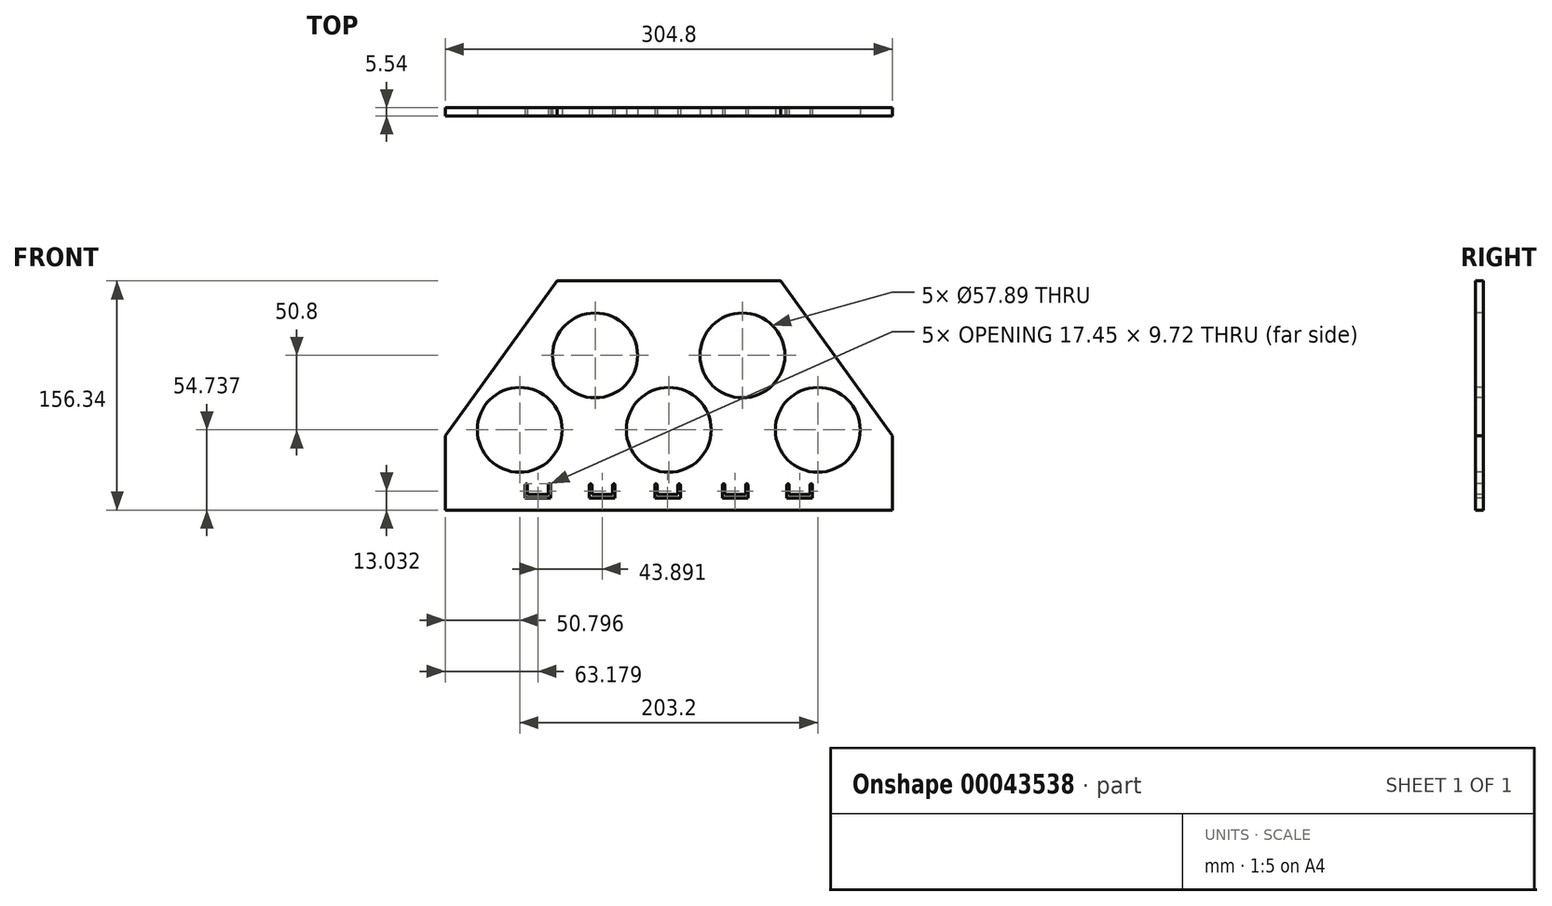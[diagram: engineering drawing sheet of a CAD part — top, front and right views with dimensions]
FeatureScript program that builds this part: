
annotation { "Feature Type Name" : "Feature", "Feature Type Description" : "" }
export const myFeature = defineFeature(function(context is Context, id is Id, definition is map)
    precondition{}
    {
        {
            var Q0;
            Q0=qCreatedBy(makeId("Front.planeOp"),FACE);
            var sketch = newSketch(context, id + "F0", { "sketchPlane" : qUnion([Q0])});
            skLineSegment(sketch, "E0", {"start": v(-67.22, 104.18) * mm, "end": v(85.18, 104.18) * mm});
            skLineSegment(sketch, "E1", {"start": v(85.18, 104.18) * mm, "end": v(161.38, -1.36) * mm});
            skLineSegment(sketch, "E2", {"start": v(161.38, -1.36) * mm, "end": v(161.38, -52.16) * mm});
            skLineSegment(sketch, "E3", {"start": v(161.38, -52.16) * mm, "end": v(-143.42, -52.16) * mm});
            skLineSegment(sketch, "E4", {"start": v(-143.42, -52.16) * mm, "end": v(-143.42, -1.36) * mm});
            skLineSegment(sketch, "E5", {"start": v(-143.42, -1.36) * mm, "end": v(-67.22, 104.18) * mm});
            skSolve(sketch);
        }
        {
            var Q0;
            Q0=makeQuery(id+"F0.imprint","IMPRINT",FACE,{"disambiguationData":[TD([[makeQuery(id+"F0.imprint","IMPRINT",EDGE,{"derivedFrom":sQuery(id+"F0.wireOp",EDGE,"E0")}),-1.0]])]});
            extrude(context, id + "F1", {"entities" : qUnion([Q0]), "depth" : 5.54 * mm});
        }
        {
            var Q0;
            Q0=makeQuery(id+"F1.opExtrude","CAP_FACE",FACE,{"disambiguationData":[OSD([sQuery(id+"F0.wireOp",EDGE,"E0"),sQuery(id+"F0.wireOp",EDGE,"E1"),sQuery(id+"F0.wireOp",EDGE,"E2"),sQuery(id+"F0.wireOp",EDGE,"E3"),sQuery(id+"F0.wireOp",EDGE,"E4"),sQuery(id+"F0.wireOp",EDGE,"E5")])],"isStart":false});
            var sketch = newSketch(context, id + "F2", { "sketchPlane" : qUnion([Q0])});
            skPoint(sketch, "E6", {"position": v(-41.24, 53.38) * mm});
            skPoint(sketch, "E7", {"position": v(59.2, 53.38) * mm});
            skPoint(sketch, "E8", {"position": v(8.98, 2.58) * mm});
            skPoint(sketch, "E9", {"position": v(-92.62, 2.58) * mm});
            skPoint(sketch, "E10", {"position": v(110.58, 2.58) * mm});
            skSolve(sketch);
        }
        {
            var Q0;
            Q0=sQuery(id+"F2.wireOp",VERTEX,"E6");
            var Q1;
            Q1=sQuery(id+"F2.wireOp",VERTEX,"E7");
            var Q2;
            Q2=sQuery(id+"F2.wireOp",VERTEX,"E10");
            var Q3;
            Q3=sQuery(id+"F2.wireOp",VERTEX,"E8");
            var Q4;
            Q4=sQuery(id+"F2.wireOp",VERTEX,"E9");
            var Q5;
            Q5=makeQuery(id+"F1.opExtrude","SWEPT_BODY",BODY,{"disambiguationData":[OSD([sQuery(id+"F0.wireOp",EDGE,"E0"),sQuery(id+"F0.wireOp",EDGE,"E1"),sQuery(id+"F0.wireOp",EDGE,"E2"),sQuery(id+"F0.wireOp",EDGE,"E3"),sQuery(id+"F0.wireOp",EDGE,"E4"),sQuery(id+"F0.wireOp",EDGE,"E5")])]});
            hole(context, id + "F3", {"style" : HoleStyle.SIMPLE, "holeDiameter" : 57.9 * mm, "endStyle" : HoleEndStyle.THROUGH, "locations" : qUnion([Q0, Q1, Q2, Q3, Q4]), "scope" : qUnion([Q5])});
        }
        {
            var Q0;
            Q0=makeQuery(id+"F1.opExtrude","CAP_FACE",FACE,{"disambiguationData":[OSD([sQuery(id+"F0.wireOp",EDGE,"E0"),sQuery(id+"F0.wireOp",EDGE,"E1"),sQuery(id+"F0.wireOp",EDGE,"E2"),sQuery(id+"F0.wireOp",EDGE,"E3"),sQuery(id+"F0.wireOp",EDGE,"E4"),sQuery(id+"F0.wireOp",EDGE,"E5")])],"isStart":false});
            var sketch = newSketch(context, id + "F4", { "sketchPlane" : qUnion([Q0])});
            skLineSegment(sketch, "E11", {"start": v(-88.97, -35.1) * mm, "end": v(-88.97, -43.99) * mm});
            skLineSegment(sketch, "E12", {"start": v(-88.97, -43.99) * mm, "end": v(-71.52, -43.99) * mm});
            skLineSegment(sketch, "E13", {"start": v(-71.52, -43.99) * mm, "end": v(-71.52, -35.1) * mm});
            skLineSegment(sketch, "E14", {"start": v(-87.32, -35.1) * mm, "end": v(-87.32, -41.6) * mm});
            skLineSegment(sketch, "E15", {"start": v(-87.32, -41.6) * mm, "end": v(-73.17, -41.6) * mm});
            skLineSegment(sketch, "E16", {"start": v(-73.17, -41.6) * mm, "end": v(-73.17, -35.1) * mm});
            skArc(sketch, "E17", {"start": v(-87.32, -35.1) * mm, "mid": v(-88.14, -34.27) * mm, "end": v(-88.97, -35.1) * mm});
            skArc(sketch, "E18", {"start": v(-71.52, -35.1) * mm, "mid": v(-72.34, -34.27) * mm, "end": v(-73.17, -35.1) * mm});
            skSolve(sketch);
        }
        {
            var Q0;
            Q0=makeQuery(id+"F4.imprint","IMPRINT",FACE,{"disambiguationData":[TD([[makeQuery(id+"F4.imprint","IMPRINT",EDGE,{"derivedFrom":sQuery(id+"F4.wireOp",EDGE,"E11")}),1.0]])]});
            extrude(context, id + "F5", {"entities" : qUnion([Q0]), "operationType" : NewBodyOperationType.REMOVE, "endBound" : BoundingType.THROUGH_ALL, "oppositeDirection" : true, "depth" : 25.4 * mm});
        }
        {
            var Q0;
            Q0=makeQuery(id+"F1.opExtrude","CAP_FACE",FACE,{"disambiguationData":[OSD([sQuery(id+"F0.wireOp",EDGE,"E0"),sQuery(id+"F0.wireOp",EDGE,"E1"),sQuery(id+"F0.wireOp",EDGE,"E2"),sQuery(id+"F0.wireOp",EDGE,"E3"),sQuery(id+"F0.wireOp",EDGE,"E4"),sQuery(id+"F0.wireOp",EDGE,"E5")])],"isStart":false});
            var sketch = newSketch(context, id + "F6", { "sketchPlane" : qUnion([Q0])});
            skLineSegment(sketch, "E19", {"start": v(-45.08, -35.1) * mm, "end": v(-45.08, -43.99) * mm});
            skLineSegment(sketch, "E20", {"start": v(-45.08, -43.99) * mm, "end": v(-27.63, -43.99) * mm});
            skLineSegment(sketch, "E21", {"start": v(-27.63, -43.99) * mm, "end": v(-27.63, -35.1) * mm});
            skLineSegment(sketch, "E22", {"start": v(-43.42, -35.1) * mm, "end": v(-43.42, -41.6) * mm});
            skLineSegment(sketch, "E23", {"start": v(-43.42, -41.6) * mm, "end": v(-29.28, -41.6) * mm});
            skLineSegment(sketch, "E24", {"start": v(-29.28, -41.6) * mm, "end": v(-29.28, -35.1) * mm});
            skArc(sketch, "E25", {"start": v(-43.42, -35.1) * mm, "mid": v(-44.25, -34.27) * mm, "end": v(-45.08, -35.1) * mm});
            skArc(sketch, "E26", {"start": v(-27.63, -35.1) * mm, "mid": v(-28.45, -34.27) * mm, "end": v(-29.28, -35.1) * mm});
            skSolve(sketch);
        }
        {
            var Q0;
            Q0=makeQuery(id+"F6.imprint","IMPRINT",FACE,{"disambiguationData":[TD([[makeQuery(id+"F6.imprint","IMPRINT",EDGE,{"derivedFrom":sQuery(id+"F6.wireOp",EDGE,"E19")}),1.0]])]});
            extrude(context, id + "F7", {"entities" : qUnion([Q0]), "operationType" : NewBodyOperationType.REMOVE, "oppositeDirection" : true, "depth" : 17.76 * mm});
        }
        {
            var Q0;
            Q0=makeQuery(id+"F1.opExtrude","CAP_FACE",FACE,{"disambiguationData":[OSD([sQuery(id+"F0.wireOp",EDGE,"E0"),sQuery(id+"F0.wireOp",EDGE,"E1"),sQuery(id+"F0.wireOp",EDGE,"E2"),sQuery(id+"F0.wireOp",EDGE,"E3"),sQuery(id+"F0.wireOp",EDGE,"E4"),sQuery(id+"F0.wireOp",EDGE,"E5")])],"isStart":false});
            var sketch = newSketch(context, id + "F8", { "sketchPlane" : qUnion([Q0])});
            skLineSegment(sketch, "E27", {"start": v(-0.57, -35.1) * mm, "end": v(-0.57, -43.99) * mm});
            skLineSegment(sketch, "E28", {"start": v(-0.57, -43.99) * mm, "end": v(16.88, -43.99) * mm});
            skLineSegment(sketch, "E29", {"start": v(16.88, -43.99) * mm, "end": v(16.88, -35.1) * mm});
            skLineSegment(sketch, "E30", {"start": v(1.08, -35.1) * mm, "end": v(1.08, -41.6) * mm});
            skLineSegment(sketch, "E31", {"start": v(1.08, -41.6) * mm, "end": v(15.22, -41.6) * mm});
            skLineSegment(sketch, "E32", {"start": v(15.22, -41.6) * mm, "end": v(15.22, -35.1) * mm});
            skArc(sketch, "E33", {"start": v(1.08, -35.1) * mm, "mid": v(0.25, -34.27) * mm, "end": v(-0.57, -35.1) * mm});
            skArc(sketch, "E34", {"start": v(16.88, -35.1) * mm, "mid": v(16.05, -34.27) * mm, "end": v(15.22, -35.1) * mm});
            skSolve(sketch);
        }
        {
            var Q0;
            Q0=makeQuery(id+"F8.imprint","IMPRINT",FACE,{"disambiguationData":[TD([[makeQuery(id+"F8.imprint","IMPRINT",EDGE,{"derivedFrom":sQuery(id+"F8.wireOp",EDGE,"E27")}),1.0]])]});
            extrude(context, id + "F9", {"entities" : qUnion([Q0]), "operationType" : NewBodyOperationType.REMOVE, "oppositeDirection" : true, "depth" : 25.4 * mm});
        }
        {
            var Q0;
            Q0=makeQuery(id+"F1.opExtrude","CAP_FACE",FACE,{"disambiguationData":[OSD([sQuery(id+"F0.wireOp",EDGE,"E0"),sQuery(id+"F0.wireOp",EDGE,"E1"),sQuery(id+"F0.wireOp",EDGE,"E2"),sQuery(id+"F0.wireOp",EDGE,"E3"),sQuery(id+"F0.wireOp",EDGE,"E4"),sQuery(id+"F0.wireOp",EDGE,"E5")])],"isStart":false});
            var sketch = newSketch(context, id + "F10", { "sketchPlane" : qUnion([Q0])});
            skLineSegment(sketch, "E35", {"start": v(45.58, -35.1) * mm, "end": v(45.58, -43.99) * mm});
            skLineSegment(sketch, "E36", {"start": v(45.58, -43.99) * mm, "end": v(63.03, -43.99) * mm});
            skLineSegment(sketch, "E37", {"start": v(63.03, -43.99) * mm, "end": v(63.03, -35.1) * mm});
            skLineSegment(sketch, "E38", {"start": v(47.23, -35.1) * mm, "end": v(47.23, -41.6) * mm});
            skLineSegment(sketch, "E39", {"start": v(47.23, -41.6) * mm, "end": v(61.38, -41.6) * mm});
            skLineSegment(sketch, "E40", {"start": v(61.38, -41.6) * mm, "end": v(61.38, -35.1) * mm});
            skArc(sketch, "E41", {"start": v(47.23, -35.1) * mm, "mid": v(46.4, -34.27) * mm, "end": v(45.58, -35.1) * mm});
            skArc(sketch, "E42", {"start": v(63.03, -35.1) * mm, "mid": v(62.2, -34.27) * mm, "end": v(61.38, -35.1) * mm});
            skSolve(sketch);
        }
        {
            var Q0;
            Q0=makeQuery(id+"F10.imprint","IMPRINT",FACE,{"disambiguationData":[TD([[makeQuery(id+"F10.imprint","IMPRINT",EDGE,{"derivedFrom":sQuery(id+"F10.wireOp",EDGE,"E35")}),1.0]])]});
            extrude(context, id + "F11", {"entities" : qUnion([Q0]), "operationType" : NewBodyOperationType.REMOVE, "oppositeDirection" : true, "depth" : 25.4 * mm});
        }
        {
            var Q0;
            Q0=makeQuery(id+"F1.opExtrude","CAP_FACE",FACE,{"disambiguationData":[OSD([sQuery(id+"F0.wireOp",EDGE,"E0"),sQuery(id+"F0.wireOp",EDGE,"E1"),sQuery(id+"F0.wireOp",EDGE,"E2"),sQuery(id+"F0.wireOp",EDGE,"E3"),sQuery(id+"F0.wireOp",EDGE,"E4"),sQuery(id+"F0.wireOp",EDGE,"E5")])],"isStart":false});
            var sketch = newSketch(context, id + "F12", { "sketchPlane" : qUnion([Q0])});
            skLineSegment(sketch, "E43", {"start": v(89.47, -35.1) * mm, "end": v(89.47, -43.99) * mm});
            skLineSegment(sketch, "E44", {"start": v(89.47, -43.99) * mm, "end": v(106.92, -43.99) * mm});
            skLineSegment(sketch, "E45", {"start": v(106.92, -43.99) * mm, "end": v(106.92, -35.1) * mm});
            skLineSegment(sketch, "E46", {"start": v(91.12, -35.1) * mm, "end": v(91.12, -41.6) * mm});
            skLineSegment(sketch, "E47", {"start": v(91.12, -41.6) * mm, "end": v(105.27, -41.6) * mm});
            skLineSegment(sketch, "E48", {"start": v(105.27, -41.6) * mm, "end": v(105.27, -35.1) * mm});
            skArc(sketch, "E49", {"start": v(91.12, -35.1) * mm, "mid": v(90.3, -34.27) * mm, "end": v(89.47, -35.1) * mm});
            skArc(sketch, "E50", {"start": v(106.92, -35.1) * mm, "mid": v(106.1, -34.27) * mm, "end": v(105.27, -35.1) * mm});
            skSolve(sketch);
        }
        {
            var Q0;
            Q0=makeQuery(id+"F12.imprint","IMPRINT",FACE,{"disambiguationData":[TD([[makeQuery(id+"F12.imprint","IMPRINT",EDGE,{"derivedFrom":sQuery(id+"F12.wireOp",EDGE,"E43")}),1.0]])]});
            extrude(context, id + "F13", {"entities" : qUnion([Q0]), "operationType" : NewBodyOperationType.REMOVE, "oppositeDirection" : true, "depth" : 25.4 * mm});
        }
    });
